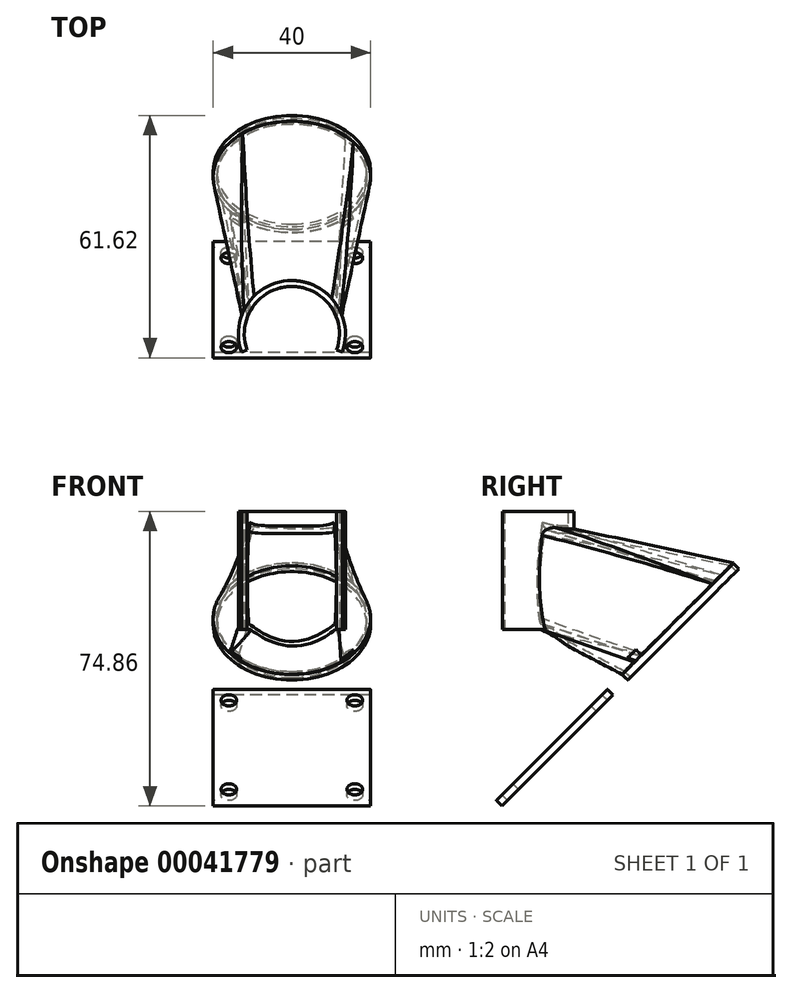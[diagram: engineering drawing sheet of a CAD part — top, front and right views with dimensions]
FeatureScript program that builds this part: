
annotation { "Feature Type Name" : "Feature", "Feature Type Description" : "" }
export const myFeature = defineFeature(function(context is Context, id is Id, definition is map)
    precondition{}
    {
        {
            var Q0;
            Q0=qCreatedBy(makeId("Front.planeOp"),FACE);
            var sketch = newSketch(context, id + "F0", { "sketchPlane" : qUnion([Q0])});
            skLineSegment(sketch, "E0.bottom", {"start": v(12.1, 19.3) * mm, "end": v(13.6, 19.3) * mm});
            skLineSegment(sketch, "E0.top", {"start": v(12.1, -10.7) * mm, "end": v(13.6, -10.7) * mm});
            skLineSegment(sketch, "E0.left", {"start": v(12.1, 19.3) * mm, "end": v(12.1, -9.35) * mm});
            skLineSegment(sketch, "E0.right", {"start": v(13.6, 19.3) * mm, "end": v(13.6, -10.7) * mm});
            skLineSegment(sketch, "E1.bottom", {"start": v(10.6, -10.7) * mm, "end": v(13.6, -10.7) * mm});
            skLineSegment(sketch, "E1.top", {"start": v(10.6, -9.35) * mm, "end": v(12.1, -9.35) * mm});
            skLineSegment(sketch, "E1.left", {"start": v(10.6, -10.7) * mm, "end": v(10.6, -9.35) * mm});
            skLineSegment(sketch, "E1.right", {"start": v(13.6, -10.7) * mm, "end": v(13.6, -9.35) * mm});
            skLineSegment(sketch, "E2", {"start": v(0, 25.12) * mm, "end": v(0, -15.88) * mm, "construction": true});
            skSolve(sketch);
        }
        {
            var Q0;
            Q0=makeQuery(id+"F0.imprint","IMPRINT",FACE,{"disambiguationData":[TD([[makeQuery(id+"F0.imprint","IMPRINT",EDGE,{"derivedFrom":sQuery(id+"F0.wireOp",EDGE,"E0.bottom")}),-1.0]])]});
            var Q1;
            Q1=sQuery(id+"F0.wireOp",EDGE,"E2");
            revolve(context, id + "F1", {"entities" : qUnion([Q0]), "axis" : qUnion([Q1]), "revolveType" : RevolveType.TWO_DIRECTIONS, "oppositeDirection" : true, "angle" : 200 * degree, "angleBack" : 340 * degree});
        }
        {
            var Q0;
            Q0=qCreatedBy(makeId("Front.planeOp"),FACE);
            cPlane(context, id + "F2", {"entities" : qUnion([Q0]), "cplaneType" : CPlaneType.OFFSET, "offset" : 1 * mm, "oppositeDirection" : true, "width" : 150 * mm, "height" : 150 * mm});
        }
        {
            var Q0;
            Q0=qCreatedBy(id+"F2.planeOp",FACE);
            var sketch = newSketch(context, id + "F3", { "sketchPlane" : qUnion([Q0])});
            skLineSegment(sketch, "E3.bottom", {"start": v(-10.57, 16.3) * mm, "end": v(10.57, 16.3) * mm});
            skLineSegment(sketch, "E3.top", {"start": v(-10.57, -7.85) * mm, "end": v(10.57, -7.85) * mm});
            skLineSegment(sketch, "E3.left", {"start": v(-10.57, 16.3) * mm, "end": v(-10.57, -7.85) * mm});
            skLineSegment(sketch, "E3.right", {"start": v(10.57, 16.3) * mm, "end": v(10.57, -7.85) * mm});
            skSolve(sketch);
        }
        {
            var Q0;
            Q0=qCreatedBy(id+"F2.planeOp",FACE);
            var sketch = newSketch(context, id + "F4", { "sketchPlane" : qUnion([Q0])});
            skLineSegment(sketch, "E4.0", {"start": v(-11.87, 17.6) * mm, "end": v(11.87, 17.6) * mm});
            skLineSegment(sketch, "E4.1", {"start": v(-11.87, 17.6) * mm, "end": v(-11.87, -9.15) * mm});
            skLineSegment(sketch, "E4.2", {"start": v(-11.87, -9.15) * mm, "end": v(11.87, -9.15) * mm});
            skLineSegment(sketch, "E4.3", {"start": v(11.87, 17.6) * mm, "end": v(11.87, -9.15) * mm});
            skSolve(sketch);
        }
        {
            var Q0;
            Q0=qCreatedBy(makeId("Front.planeOp"),FACE);
            cPlane(context, id + "F5", {"entities" : qUnion([Q0]), "cplaneType" : CPlaneType.OFFSET, "offset" : 40 * mm, "oppositeDirection" : true, "width" : 150 * mm, "height" : 150 * mm});
        }
        {
            var Q0;
            Q0=qCreatedBy(id+"F5.planeOp",FACE);
            var sketch = newSketch(context, id + "F6", { "sketchPlane" : qUnion([Q0])});
            skCircle(sketch, "E5", {"center": v(0, 0) * mm, "radius": 19 * mm});
            skCircle(sketch, "E6", {"center": v(0, 0) * mm, "radius": 20 * mm});
            skLineSegment(sketch, "E7", {"start": v(29.45, 0) * mm, "end": v(-29.25, 0) * mm, "construction": true});
            skSolve(sketch);
        }
        {
            var Q0;
            Q0 = qSketchRegion(id + "F6", true);
            extrude(context, id + "F7", {"entities" : qUnion([Q0]), "oppositeDirection" : true, "depth" : 2 * mm});
        }
        {
            var Q0;
            Q0=makeQuery(id+"F7.opExtrude","SWEPT_BODY",BODY,{"disambiguationData":[OSD([sQuery(id+"F6.wireOp",EDGE,"E5"),sQuery(id+"F6.wireOp",EDGE,"E6")])]});
            var Q1;
            Q1=sQuery(id+"F6.wireOp",EDGE,"E7");
            transform(context, id + "F8", {"entities" : qUnion([Q0]), "transformType" : TransformType.ROTATION, "transformAxis" : qUnion([Q1]), "angle" : 45 * degree, "makeCopy" : false});
        }
        {
            var Q0;
            Q0=makeQuery(id+"F7.opExtrude","SWEPT_BODY",BODY,{"disambiguationData":[OSD([sQuery(id+"F6.wireOp",EDGE,"E5"),sQuery(id+"F6.wireOp",EDGE,"E6")])]});
            transform(context, id + "F9", {"entities" : qUnion([Q0]), "transformType" : TransformType.TRANSLATION_3D, "dx" : 0 * mm, "dy" : 0 * mm, "dz" : 0 * mm, "makeCopy" : false});
        }
        {
            var Q0;
            Q0=makeQuery(id+"F7.opExtrude","SWEPT_BODY",BODY,{"disambiguationData":[OSD([sQuery(id+"F6.wireOp",EDGE,"E5"),sQuery(id+"F6.wireOp",EDGE,"E6")])]});
            transform(context, id + "F10", {"entities" : qUnion([Q0]), "transformType" : TransformType.TRANSLATION_3D, "dx" : 0 * mm, "dy" : 0 * mm, "dz" : -8 * mm, "makeCopy" : false});
        }
        {
            var Q0;
            Q0=makeQuery(id+"F7.opExtrude","CAP_FACE",FACE,{"disambiguationData":[OSD([sQuery(id+"F6.wireOp",EDGE,"E5"),sQuery(id+"F6.wireOp",EDGE,"E6")])],"isStart":true});
            var sketch = newSketch(context, id + "F11", { "sketchPlane" : qUnion([Q0])});
            skCircle(sketch, "E8", {"center": v(0, 22.63) * mm, "radius": 20 * mm});
            skSolve(sketch);
        }
        {
            var Q0;
            Q0 = qSketchRegion(id + "F11", true);
            extrude(context, id + "F12", {"entities" : qUnion([Q0]), "depth" : 0.1 * mm});
        }
        {
            var Q1;
            Q1=makeQuery(id+"F12.opExtrude","CAP_FACE",FACE,{"disambiguationData":[OSD([sQuery(id+"F11.wireOp",EDGE,"E8")])],"isStart":false});
            var Q2;
            Q2=makeQuery(id+"F4.imprint","IMPRINT",FACE,{"disambiguationData":[TD([[makeQuery(id+"F4.imprint","IMPRINT",EDGE,{"derivedFrom":sQuery(id+"F4.wireOp",EDGE,"E4.0")}),-1.0]])]});
            loft(context, id + "F13", {"operationType" : NewBodyOperationType.ADD, "sheetProfilesArray" : [{ "sheetProfileEntities" : qUnion([Q1]) }, { "sheetProfileEntities" : qUnion([Q2]) }]});
        }
        {
            var Q0;
            Q0=makeQuery(id+"F11.imprint","IMPRINT",FACE,{"disambiguationData":[TD([[makeQuery(id+"F11.imprint","IMPRINT",EDGE,{"derivedFrom":makeQuery(id+"F7.opExtrude","CAP_EDGE",EDGE,{"disambiguationData":[OSD([sQuery(id+"F6.wireOp",EDGE,"E5")])],"isStart":true})}),1.0]])]});
            var Q1;
            Q1=makeQuery(id+"F3.imprint","IMPRINT",FACE,{"disambiguationData":[TD([[makeQuery(id+"F3.imprint","IMPRINT",EDGE,{"derivedFrom":sQuery(id+"F3.wireOp",EDGE,"E3.bottom")}),-1.0]])]});
            loft(context, id + "F14", {"operationType" : NewBodyOperationType.REMOVE, "sheetProfilesArray" : [{ "sheetProfileEntities" : qUnion([Q0]) }, { "sheetProfileEntities" : qUnion([Q1]) }]});
        }
        {
            var Q0;
            Q0=makeQuery(id+"F7.opExtrude","CAP_FACE",FACE,{"disambiguationData":[OSD([sQuery(id+"F6.wireOp",EDGE,"E5"),sQuery(id+"F6.wireOp",EDGE,"E6")])],"isStart":false});
            var sketch = newSketch(context, id + "F15", { "sketchPlane" : qUnion([Q0])});
            skLineSegment(sketch, "E9.rect.bottom", {"start": v(-20, -42.63) * mm, "end": v(20, -42.63) * mm});
            skLineSegment(sketch, "E9.rect.top", {"start": v(-20, -2.63) * mm, "end": v(20, -2.63) * mm});
            skLineSegment(sketch, "E9.rect.left", {"start": v(-20, -42.63) * mm, "end": v(-20, -2.63) * mm});
            skLineSegment(sketch, "E9.rect.right", {"start": v(20, -42.63) * mm, "end": v(20, -2.63) * mm});
            skPoint(sketch, "E9.rect.middle", {"position": v(0, -22.63) * mm});
            skSolve(sketch);
        }
        {
            var Q0;
            Q0 = qSketchRegion(id + "F15", true);
            extrude(context, id + "F16", {"entities" : qUnion([Q0]), "operationType" : NewBodyOperationType.ADD, "oppositeDirection" : true, "depth" : 2 * mm});
        }
        {
            var Q0;
            Q0=sQuery(id+"F11.wireOp",VERTEX,"E8.center");
            var Q1;
            Q1=makeQuery(id+"F7.opExtrude","SWEPT_BODY",BODY,{"disambiguationData":[OSD([sQuery(id+"F6.wireOp",EDGE,"E5"),sQuery(id+"F6.wireOp",EDGE,"E6")])]});
            hole(context, id + "F17", {"style" : HoleStyle.SIMPLE, "holeDiameter" : 37 * mm, "endStyle" : HoleEndStyle.THROUGH, "locations" : qUnion([Q0]), "scope" : qUnion([Q1])});
        }
        {
            var Q0;
            Q0=makeQuery(id+"F16.boolean.opBoolean","MERGE",FACE,{"derivedFrom":[makeQuery(id+"F7.opExtrude","CAP_FACE",FACE,{"disambiguationData":[OSD([sQuery(id+"F6.wireOp",EDGE,"E5"),sQuery(id+"F6.wireOp",EDGE,"E6")])],"isStart":false}),makeQuery(id+"F16.opExtrude","CAP_FACE",FACE,{"disambiguationData":[OSD([sQuery(id+"F15.wireOp",EDGE,"E9.rect.bottom"),sQuery(id+"F15.wireOp",EDGE,"E9.rect.top"),sQuery(id+"F15.wireOp",EDGE,"E9.rect.left"),sQuery(id+"F15.wireOp",EDGE,"E9.rect.right")])],"isStart":true})]});
            var sketch = newSketch(context, id + "F18", { "sketchPlane" : qUnion([Q0])});
            skCircle(sketch, "E10", {"center": v(16, -38.63) * mm, "radius": 2 * mm});
            skCircle(sketch, "E11", {"center": v(-16, -38.63) * mm, "radius": 2 * mm});
            skCircle(sketch, "E12", {"center": v(-16, -6.63) * mm, "radius": 2 * mm});
            skCircle(sketch, "E13", {"center": v(16, -6.63) * mm, "radius": 2 * mm});
            skSolve(sketch);
        }
        {
            var Q0;
            Q0 = qSketchRegion(id + "F18", true);
            extrude(context, id + "F19", {"entities" : qUnion([Q0]), "operationType" : NewBodyOperationType.REMOVE, "oppositeDirection" : true, "depth" : 2 * mm});
        }
        {
            var Q0;
            Q0=makeQuery(id+"F13.opLoft","SWEPT_EDGE",EDGE,{"disambiguationData":[OSD([sQuery(id+"F4.wireOp",EDGE,"E4.0"),sQuery(id+"F4.wireOp",EDGE,"E4.1"),sQuery(id+"F4.wireOp",EDGE,"E4.2")])]});
            var Q1;
            Q1=makeQuery(id+"F13.opLoft","SWEPT_EDGE",EDGE,{"disambiguationData":[OSD([sQuery(id+"F4.wireOp",EDGE,"E4.1"),sQuery(id+"F4.wireOp",EDGE,"E4.2"),sQuery(id+"F4.wireOp",EDGE,"E4.3"),sQuery(id+"F11.wireOp",EDGE,"E8")])]});
            var Q2;
            Q2=makeQuery(id+"F13.opLoft","SWEPT_EDGE",EDGE,{"disambiguationData":[OSD([sQuery(id+"F4.wireOp",EDGE,"E4.0"),sQuery(id+"F4.wireOp",EDGE,"E4.2"),sQuery(id+"F4.wireOp",EDGE,"E4.3"),sQuery(id+"F11.wireOp",EDGE,"E8")])]});
            var Q3;
            Q3=makeQuery(id+"F13.opLoft","SWEPT_EDGE",EDGE,{"disambiguationData":[OSD([sQuery(id+"F4.wireOp",EDGE,"E4.0"),sQuery(id+"F4.wireOp",EDGE,"E4.1"),sQuery(id+"F4.wireOp",EDGE,"E4.3"),sQuery(id+"F11.wireOp",EDGE,"E8")])]});
            fillet(context, id + "F20", {"entities" : qUnion([Q0, Q1, Q2, Q3]), "radius" : 3 * mm, "tangentPropagation" : true, "allowEdgeOverflow" : false});
        }
        {
            var Q0;
            Q0=makeQuery(id+"F16.opExtrude","CAP_EDGE",EDGE,{"disambiguationData":[OSD([sQuery(id+"F15.wireOp",EDGE,"E9.rect.bottom")])],"isStart":false});
            var Q1;
            Q1=makeQuery(id+"F16.opExtrude","CAP_EDGE",EDGE,{"disambiguationData":[OSD([sQuery(id+"F15.wireOp",EDGE,"E9.rect.left")])],"isStart":false});
            var Q2;
            Q2=makeQuery(id+"F16.opExtrude","CAP_EDGE",EDGE,{"disambiguationData":[OSD([sQuery(id+"F15.wireOp",EDGE,"E9.rect.top")])],"isStart":false});
            var Q3;
            Q3=makeQuery(id+"F16.opExtrude","CAP_EDGE",EDGE,{"disambiguationData":[OSD([sQuery(id+"F15.wireOp",EDGE,"E9.rect.right")])],"isStart":false});
            fillet(context, id + "F21", {"entities" : qUnion([Q0, Q1, Q2, Q3]), "radius" : 0.2 * mm, "tangentPropagation" : true, "allowEdgeOverflow" : false});
        }
        {
            var Q0;
            Q0=makeQuery(id+"F1.opRevolve","SWEPT_FACE",FACE,{"disambiguationData":[OSD([sQuery(id+"F0.wireOp",EDGE,"E0.bottom")])]});
            var sketch = newSketch(context, id + "F22", { "sketchPlane" : qUnion([Q0])});
            skCircle(sketch, "E14", {"center": v(0, 0) * mm, "radius": 12.1 * mm});
            skSolve(sketch);
        }
        {
            var Q0;
            Q0 = qSketchRegion(id + "F22", true);
            extrude(context, id + "F23", {"entities" : qUnion([Q0]), "operationType" : NewBodyOperationType.REMOVE, "oppositeDirection" : true, "depth" : 40 * mm});
        }
        {
            var Q0;
            {var subQ0=sQuery(id+"F3.wireOp",EDGE,"E3.bottom");var subQ1=sQuery(id+"F3.wireOp",EDGE,"E3.top");var subQ2=sQuery(id+"F3.wireOp",EDGE,"E3.left");var subQ3=sQuery(id+"F3.wireOp",EDGE,"E3.right");var subQ4=sQuery(id+"F6.wireOp",EDGE,"E5");Q0=makeQuery(id+"F23.boolean.opBoolean","INTERSECT",EDGE,{"derivedFrom":[makeQuery(id+"F14.boolean.opBoolean","COPY",FACE,{"disambiguationData":[OD(0.0)],"derivedFrom":makeQuery(id+"F14.opLoft","SWEPT_FACE",FACE,{"disambiguationData":[OSD([subQ0,subQ1,subQ2,subQ3,subQ4]),TDD([makeQuery(id+"F3.imprint","INTERSECT",VERTEX,{"derivedFrom":[subQ0,subQ2]}),makeQuery(id+"F3.imprint","INTERSECT",VERTEX,{"derivedFrom":[subQ0,subQ3]}),makeQuery(id+"F3.imprint","INTERSECT",VERTEX,{"derivedFrom":[subQ1,subQ3]}),makeQuery(id+"F3.imprint","IMPRINT",EDGE,{"derivedFrom":subQ0}),makeQuery(id+"F11.imprint","IMPRINT",EDGE,{"derivedFrom":makeQuery(id+"F7.opExtrude","CAP_EDGE",EDGE,{"disambiguationData":[OSD([subQ4])],"isStart":true})})])]})}),makeQuery(id+"F23.opExtrude","SWEPT_FACE",FACE,{"disambiguationData":[OSD([sQuery(id+"F22.wireOp",EDGE,"E14")])]})]});}
            fillet(context, id + "F24", {"entities" : qUnion([Q0]), "radius" : 2 * mm, "tangentPropagation" : true, "allowEdgeOverflow" : false});
        }
        {
            var Q0;
            Q0=makeQuery(id+"F1.opRevolve","CAP_EDGE",EDGE,{"disambiguationData":[OSD([sQuery(id+"F0.wireOp",EDGE,"E0.right"),sQuery(id+"F0.wireOp",EDGE,"E1.right")])],"isStart":true});
            chamfer(context, id + "F25", {"entities" : qUnion([Q0]), "chamferType" : ChamferType.TWO_OFFSETS, "width1" : 0.1 * mm, "oppositeDirection" : false, "width2" : 5 * mm, "tangentPropagation" : true});
        }
        {
            var Q0;
            Q0=makeQuery(id+"F1.opRevolve","CAP_EDGE",EDGE,{"disambiguationData":[OSD([sQuery(id+"F0.wireOp",EDGE,"E0.right"),sQuery(id+"F0.wireOp",EDGE,"E1.right")])],"isStart":false});
            chamfer(context, id + "F26", {"entities" : qUnion([Q0]), "chamferType" : ChamferType.TWO_OFFSETS, "width1" : 0.1 * mm, "oppositeDirection" : true, "width2" : 5 * mm, "tangentPropagation" : true});
        }
        {
            var Q0;
            Q0=makeQuery(id+"F16.boolean.opBoolean","MERGE",FACE,{"derivedFrom":[makeQuery(id+"F7.opExtrude","CAP_FACE",FACE,{"disambiguationData":[OSD([sQuery(id+"F6.wireOp",EDGE,"E5"),sQuery(id+"F6.wireOp",EDGE,"E6")])],"isStart":true}),makeQuery(id+"F16.opExtrude","CAP_FACE",FACE,{"disambiguationData":[OSD([sQuery(id+"F15.wireOp",EDGE,"E9.rect.bottom"),sQuery(id+"F15.wireOp",EDGE,"E9.rect.top"),sQuery(id+"F15.wireOp",EDGE,"E9.rect.left"),sQuery(id+"F15.wireOp",EDGE,"E9.rect.right")])],"isStart":false})]});
            var sketch = newSketch(context, id + "F27", { "sketchPlane" : qUnion([Q0])});
            skCircle(sketch, "E15.0", {"center": v(16, 6.63) * mm, "radius": 3 * mm});
            skCircle(sketch, "E16.0", {"center": v(-16, 6.63) * mm, "radius": 3 * mm});
            skSolve(sketch);
        }
        {
            var Q0;
            Q0 = qSketchRegion(id + "F27", true);
            extrude(context, id + "F28", {"entities" : qUnion([Q0]), "operationType" : NewBodyOperationType.REMOVE, "depth" : 2 * mm});
        }
    });
